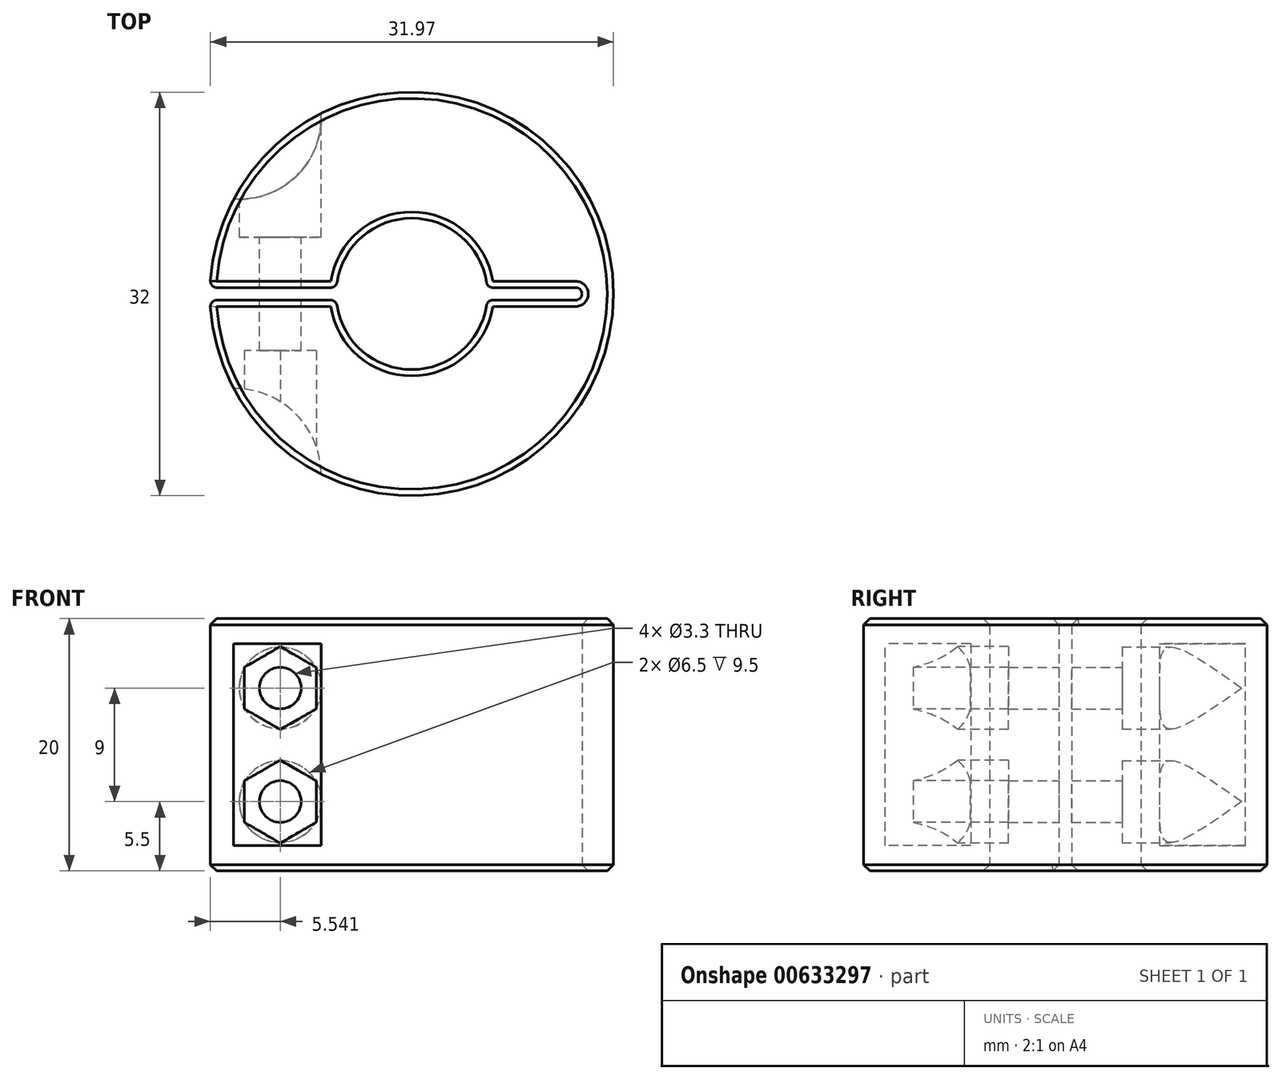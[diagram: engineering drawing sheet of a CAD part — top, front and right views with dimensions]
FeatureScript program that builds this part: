
annotation { "Feature Type Name" : "Feature", "Feature Type Description" : "" }
export const myFeature = defineFeature(function(context is Context, id is Id, definition is map)
    precondition{}
    {
        {
            var Q0;
            Q0=qCreatedBy(makeId("Top.planeOp"),FACE);
            var sketch = newSketch(context, id + "F0", { "sketchPlane" : qUnion([Q0])});
            skArc(sketch, "E0", {"start": v(5.93, 0.92) * mm, "mid": v(0, 6) * mm, "end": v(-5.93, 0.92) * mm});
            skArc(sketch, "E1.0", {"start": v(-15.97, -1.03) * mm, "mid": v(16, 0) * mm, "end": v(-15.97, 1.03) * mm});
            skLineSegment(sketch, "E2", {"start": v(6.42, 0.5) * mm, "end": v(13, 0.5) * mm});
            skLineSegment(sketch, "E3", {"start": v(13.5, 0) * mm, "end": v(13.5, 0) * mm});
            skLineSegment(sketch, "E4", {"start": v(13, -0.5) * mm, "end": v(6.42, -0.5) * mm});
            skPoint(sketch, "E5.visualSharp", {"position": v(13.5, 0.5) * mm});
            skArc(sketch, "E5.filletArc", {"start": v(13.5, 0) * mm, "mid": v(13.35, 0.35) * mm, "end": v(13, 0.5) * mm});
            skPoint(sketch, "E6.visualSharp", {"position": v(13.5, -0.5) * mm});
            skArc(sketch, "E6.filletArc", {"start": v(13, -0.5) * mm, "mid": v(13.35, -0.35) * mm, "end": v(13.5, 0) * mm});
            skPoint(sketch, "E7.visualSharp", {"position": v(5.98, 0.5) * mm});
            skArc(sketch, "E7.filletArc", {"start": v(5.93, 0.92) * mm, "mid": v(6.1, 0.62) * mm, "end": v(6.42, 0.5) * mm});
            skPoint(sketch, "E8.visualSharp", {"position": v(5.98, -0.5) * mm});
            skArc(sketch, "E8.filletArc", {"start": v(6.42, -0.5) * mm, "mid": v(6.1, -0.62) * mm, "end": v(5.93, -0.92) * mm});
            skLineSegment(sketch, "E9", {"start": v(-6.42, 0.5) * mm, "end": v(-15.47, 0.5) * mm});
            skLineSegment(sketch, "E10", {"start": v(-15.47, -0.5) * mm, "end": v(-6.42, -0.5) * mm});
            skArc(sketch, "E11.trimOffspring", {"start": v(-5.93, -0.92) * mm, "mid": v(0, -6) * mm, "end": v(5.93, -0.92) * mm});
            skPoint(sketch, "E12.visualSharp", {"position": v(-16, 0.5) * mm});
            skArc(sketch, "E12.filletArc", {"start": v(-15.97, 1.03) * mm, "mid": v(-15.83, 0.66) * mm, "end": v(-15.47, 0.5) * mm});
            skPoint(sketch, "E13.visualSharp", {"position": v(-16, -0.5) * mm});
            skArc(sketch, "E13.filletArc", {"start": v(-15.47, -0.5) * mm, "mid": v(-15.83, -0.66) * mm, "end": v(-15.97, -1.03) * mm});
            skPoint(sketch, "E14.visualSharp", {"position": v(-5.98, 0.5) * mm});
            skArc(sketch, "E14.filletArc", {"start": v(-6.42, 0.5) * mm, "mid": v(-6.1, 0.62) * mm, "end": v(-5.93, 0.92) * mm});
            skPoint(sketch, "E15.visualSharp", {"position": v(-5.98, -0.5) * mm});
            skArc(sketch, "E15.filletArc", {"start": v(-5.93, -0.92) * mm, "mid": v(-6.1, -0.62) * mm, "end": v(-6.42, -0.5) * mm});
            skSolve(sketch);
        }
        {
            var Q0;
            Q0=makeQuery(id+"F0.imprint","IMPRINT",FACE,{"disambiguationData":[TD([[makeQuery(id+"F0.imprint","IMPRINT",EDGE,{"derivedFrom":sQuery(id+"F0.wireOp",EDGE,"E0")}),-1.0]])]});
            extrude(context, id + "F1", {"entities" : qUnion([Q0]), "depth" : 20 * mm, "offsetDistance" : 25 * mm});
        }
        {
            var Q0;
            Q0=makeQuery(id+"F1.opExtrude","CAP_FACE",FACE,{"disambiguationData":[OSD([sQuery(id+"F0.wireOp",EDGE,"E0"),sQuery(id+"F0.wireOp",EDGE,"E1.0"),sQuery(id+"F0.wireOp",EDGE,"E2"),sQuery(id+"F0.wireOp",EDGE,"E4"),sQuery(id+"F0.wireOp",EDGE,"E5.filletArc"),sQuery(id+"F0.wireOp",EDGE,"E6.filletArc"),sQuery(id+"F0.wireOp",EDGE,"E7.filletArc"),sQuery(id+"F0.wireOp",EDGE,"E8.filletArc"),sQuery(id+"F0.wireOp",EDGE,"E9"),sQuery(id+"F0.wireOp",EDGE,"E10"),sQuery(id+"F0.wireOp",EDGE,"E11.trimOffspring"),sQuery(id+"F0.wireOp",EDGE,"E12.filletArc"),sQuery(id+"F0.wireOp",EDGE,"E13.filletArc"),sQuery(id+"F0.wireOp",EDGE,"E14.filletArc"),sQuery(id+"F0.wireOp",EDGE,"E15.filletArc")])],"isStart":false});
            var sketch = newSketch(context, id + "F2", { "sketchPlane" : qUnion([Q0])});
            skLineSegment(sketch, "E16.bottom", {"start": v(-13.68, 7.5) * mm, "end": v(-7.18, 7.5) * mm, "construction": true});
            skLineSegment(sketch, "E16.top", {"start": v(-13.68, 4.5) * mm, "end": v(-7.18, 4.5) * mm, "construction": true});
            skLineSegment(sketch, "E16.left", {"start": v(-13.68, 7.5) * mm, "end": v(-13.68, 4.5) * mm, "construction": true});
            skLineSegment(sketch, "E16.right", {"start": v(-7.18, 7.5) * mm, "end": v(-7.18, 4.5) * mm, "construction": true});
            skLineSegment(sketch, "E17.bottom", {"start": v(-11.93, 4.5) * mm, "end": v(-8.93, 4.5) * mm, "construction": true});
            skLineSegment(sketch, "E17.top", {"start": v(-11.93, -7.5) * mm, "end": v(-8.93, -7.5) * mm, "construction": true});
            skLineSegment(sketch, "E17.left", {"start": v(-11.93, 4.5) * mm, "end": v(-11.93, -7.5) * mm, "construction": true});
            skLineSegment(sketch, "E17.right", {"start": v(-8.93, 4.5) * mm, "end": v(-8.93, -7.5) * mm, "construction": true});
            skLineSegment(sketch, "E18", {"start": v(-10.43, -7.5) * mm, "end": v(-10.43, 6.38) * mm, "construction": true});
            skLineSegment(sketch, "E19", {"start": v(-13.68, -4.5) * mm, "end": v(-6.68, -4.5) * mm, "construction": true});
            skPoint(sketch, "E19.startSnap0", {"position": v(-13.68, 6) * mm});
            skLineSegment(sketch, "E20.bottom", {"start": v(-7.18, 7.5) * mm, "end": v(-15.38, 7.5) * mm});
            skLineSegment(sketch, "E20.top", {"start": v(-7.18, 14.57) * mm, "end": v(-15.38, 14.57) * mm});
            skLineSegment(sketch, "E20.left", {"start": v(-7.18, 7.5) * mm, "end": v(-7.18, 14.57) * mm});
            skLineSegment(sketch, "E20.right", {"start": v(-15.38, 7.5) * mm, "end": v(-15.38, 14.57) * mm});
            skLineSegment(sketch, "E21.bottom", {"start": v(-7.18, -7.5) * mm, "end": v(-17.74, -7.5) * mm});
            skLineSegment(sketch, "E21.top", {"start": v(-7.18, -14.68) * mm, "end": v(-17.74, -14.68) * mm});
            skLineSegment(sketch, "E21.left", {"start": v(-7.18, -7.5) * mm, "end": v(-7.18, -14.68) * mm});
            skLineSegment(sketch, "E21.right", {"start": v(-17.74, -7.5) * mm, "end": v(-17.74, -14.68) * mm});
            skSolve(sketch);
        }
        {
            var Q0;
            {var subQ0=sQuery(id+"F2.wireOp",EDGE,"E20.left");var subQ1=sQuery(id+"F2.wireOp",EDGE,"E20.bottom");var subQ2=makeQuery(id+"F2.imprint","INTERSECT",VERTEX,{"derivedFrom":[subQ1,subQ0]});Q0=makeQuery(id+"F2.imprint","IMPRINT",FACE,{"disambiguationData":[TD([[makeQuery(id+"F2.imprint","IMPRINT",EDGE,{"disambiguationData":[TD([[subQ2,-1.0]])],"derivedFrom":subQ1}),-1.0]])]});}
            var Q1;
            {var subQ0=sQuery(id+"F2.wireOp",EDGE,"E21.left");var subQ1=sQuery(id+"F2.wireOp",EDGE,"E21.bottom");var subQ2=makeQuery(id+"F2.imprint","INTERSECT",VERTEX,{"derivedFrom":[subQ1,subQ0]});Q1=makeQuery(id+"F2.imprint","IMPRINT",FACE,{"disambiguationData":[TD([[makeQuery(id+"F2.imprint","IMPRINT",EDGE,{"disambiguationData":[TD([[subQ2,-1.0]])],"derivedFrom":subQ1}),1.0]])]});}
            extrude(context, id + "F3", {"entities" : qUnion([Q0, Q1]), "operationType" : NewBodyOperationType.REMOVE, "oppositeDirection" : true, "depth" : 18 * mm, "offsetDistance" : 25 * mm, "hasSecondDirection" : true, "secondDirectionOppositeDirection" : true, "secondDirectionDepth" : 2 * mm});
        }
        {
            var Q0;
            Q0=makeQuery(id+"F3.boolean.opBoolean","COPY",FACE,{"derivedFrom":makeQuery(id+"F3.opExtrude","SWEPT_FACE",FACE,{"disambiguationData":[OSD([sQuery(id+"F2.wireOp",EDGE,"E20.bottom")])]})});
            var sketch = newSketch(context, id + "F4", { "sketchPlane" : qUnion([Q0])});
            skLineSegment(sketch, "E22", {"start": v(10.43, 18) * mm, "end": v(10.43, 2) * mm, "construction": true});
            skPoint(sketch, "E23", {"position": v(10.43, 14.5) * mm});
            skPoint(sketch, "E24", {"position": v(10.43, 5.5) * mm});
            skSolve(sketch);
        }
        {
            var Q0;
            Q0=sQuery(id+"F4.wireOp",VERTEX,"E23");
            var Q1;
            Q1=sQuery(id+"F4.wireOp",VERTEX,"E24");
            var Q2;
            Q2=makeQuery(id+"F1.opExtrude","SWEPT_BODY",BODY,{"disambiguationData":[OSD([sQuery(id+"F0.wireOp",EDGE,"E0"),sQuery(id+"F0.wireOp",EDGE,"E1.0"),sQuery(id+"F0.wireOp",EDGE,"E2"),sQuery(id+"F0.wireOp",EDGE,"E4"),sQuery(id+"F0.wireOp",EDGE,"E5.filletArc"),sQuery(id+"F0.wireOp",EDGE,"E6.filletArc"),sQuery(id+"F0.wireOp",EDGE,"E7.filletArc"),sQuery(id+"F0.wireOp",EDGE,"E8.filletArc"),sQuery(id+"F0.wireOp",EDGE,"E9"),sQuery(id+"F0.wireOp",EDGE,"E10"),sQuery(id+"F0.wireOp",EDGE,"E11.trimOffspring"),sQuery(id+"F0.wireOp",EDGE,"E12.filletArc"),sQuery(id+"F0.wireOp",EDGE,"E13.filletArc"),sQuery(id+"F0.wireOp",EDGE,"E14.filletArc"),sQuery(id+"F0.wireOp",EDGE,"E15.filletArc")])]});
            hole(context, id + "F5", {"style" : HoleStyle.C_BORE, "endStyle" : HoleEndStyle.THROUGH, "standardTappedOrClearance" : lookupTablePath({ "standard" : "ISO", "fit" : "Normal", "size" : "M3", "type" : "Clearance" }), "standardBlindInLast" : lookupTablePath({ "fit" : "Standard", "standard" : "ISO", "size" : "M3", "type" : "Clearance" }), "holeDiameter" : 3.3 * mm, "cBoreDiameter" : 6.5 * mm, "cBoreDepth" : 3 * mm, "majorDiameter" : 5 * mm, "isTappedThrough" : true, "tappedDepth" : 15 * mm, "tapClearance" : 0, "startFromSketch" : true, "locations" : qUnion([Q0, Q1]), "scope" : qUnion([Q2])});
        }
        {
            var Q0;
            Q0=makeQuery(id+"F3.boolean.opBoolean","COPY",FACE,{"derivedFrom":makeQuery(id+"F3.opExtrude","SWEPT_FACE",FACE,{"disambiguationData":[OSD([sQuery(id+"F2.wireOp",EDGE,"E21.bottom")])]})});
            var sketch = newSketch(context, id + "F6", { "sketchPlane" : qUnion([Q0])});
            skCircle(sketch, "E25.cCircle", {"center": v(-10.43, 14.5) * mm, "radius": 2.85 * mm, "construction": true});
            skLineSegment(sketch, "E25.0", {"start": v(-13.28, 12.85) * mm, "end": v(-13.28, 16.15) * mm});
            skLineSegment(sketch, "E25.1", {"start": v(-13.28, 16.15) * mm, "end": v(-10.43, 17.8) * mm});
            skLineSegment(sketch, "E25.2", {"start": v(-10.43, 17.8) * mm, "end": v(-7.58, 16.15) * mm});
            skLineSegment(sketch, "E25.3", {"start": v(-7.58, 16.15) * mm, "end": v(-7.58, 12.85) * mm});
            skLineSegment(sketch, "E25.4", {"start": v(-7.58, 12.85) * mm, "end": v(-10.43, 11.2) * mm});
            skLineSegment(sketch, "E25.5", {"start": v(-10.43, 11.2) * mm, "end": v(-13.28, 12.85) * mm});
            skPoint(sketch, "E25.0.midPoint", {"position": v(-13.28, 14.5) * mm});
            skCircle(sketch, "E26.cCircle", {"center": v(-10.43, 5.5) * mm, "radius": 2.85 * mm, "construction": true});
            skLineSegment(sketch, "E26.0", {"start": v(-13.28, 3.85) * mm, "end": v(-13.28, 7.15) * mm});
            skLineSegment(sketch, "E26.1", {"start": v(-13.28, 7.15) * mm, "end": v(-10.43, 8.8) * mm});
            skLineSegment(sketch, "E26.2", {"start": v(-10.43, 8.8) * mm, "end": v(-7.58, 7.15) * mm});
            skLineSegment(sketch, "E26.3", {"start": v(-7.58, 7.15) * mm, "end": v(-7.58, 3.85) * mm});
            skLineSegment(sketch, "E26.4", {"start": v(-7.58, 3.85) * mm, "end": v(-10.43, 2.2) * mm});
            skLineSegment(sketch, "E26.5", {"start": v(-10.43, 2.2) * mm, "end": v(-13.28, 3.85) * mm});
            skPoint(sketch, "E26.0.midPoint", {"position": v(-13.28, 5.5) * mm});
            skSolve(sketch);
        }
        {
            var Q0;
            Q0=makeQuery(id+"F6.imprint","IMPRINT",FACE,{"disambiguationData":[TD([[makeQuery(id+"F6.imprint","IMPRINT",EDGE,{"derivedFrom":sQuery(id+"F6.wireOp",EDGE,"E25.0")}),-1.0]])]});
            var Q1;
            Q1=makeQuery(id+"F6.imprint","IMPRINT",FACE,{"disambiguationData":[TD([[makeQuery(id+"F6.imprint","IMPRINT",EDGE,{"derivedFrom":sQuery(id+"F6.wireOp",EDGE,"E26.0")}),-1.0]])]});
            extrude(context, id + "F7", {"entities" : qUnion([Q0, Q1]), "operationType" : NewBodyOperationType.REMOVE, "oppositeDirection" : true, "depth" : 3 * mm, "offsetDistance" : 25 * mm});
        }
        {
            var Q0;
            {var subQ0=sQuery(id+"F2.wireOp",EDGE,"E20.bottom");var subQ2=sQuery(id+"F2.wireOp",EDGE,"E20.left");var subQ4=makeQuery(id+"F5.hole-0.opRevolve","SWEPT_FACE",FACE,{"disambiguationData":[OSD([sQuery(id+"F5.hole-0.sketch.wireOp",EDGE,"cbore_start_line_2")])]});Q0=makeQuery(id+"F5.hole-1.boolean.opBoolean","SPLIT",EDGE,{"disambiguationData":[TD([makeQuery(id+"F5.hole-0.boolean.opBoolean","COPY",FACE,{"derivedFrom":subQ4})])],"derivedFrom":makeQuery(id+"F5.hole-0.boolean.opBoolean","SPLIT",EDGE,{"disambiguationData":[TD([makeQuery(id+"F3.boolean.opBoolean","COPY",FACE,{"derivedFrom":makeQuery(id+"F3.opExtrude","CAP_FACE",FACE,{"disambiguationData":[OSD([sQuery(id+"F0.wireOp",EDGE,"E1.0"),subQ0,subQ2])],"isStart":false})})])],"derivedFrom":makeQuery(id+"F3.boolean.opBoolean","COPY",EDGE,{"derivedFrom":makeQuery(id+"F3.opExtrude","SWEPT_EDGE",EDGE,{"disambiguationData":[OSD([subQ0,subQ2])]})})})});}
            var Q1;
            {var subQ0=sQuery(id+"F2.wireOp",EDGE,"E20.bottom");var subQ1=sQuery(id+"F2.wireOp",EDGE,"E20.left");Q1=makeQuery(id+"F5.hole-0.boolean.opBoolean","SPLIT",EDGE,{"disambiguationData":[TD([makeQuery(id+"F3.boolean.opBoolean","COPY",FACE,{"derivedFrom":makeQuery(id+"F3.opExtrude","CAP_FACE",FACE,{"disambiguationData":[OSD([sQuery(id+"F0.wireOp",EDGE,"E1.0"),subQ0,subQ1])],"isStart":true})})])],"derivedFrom":makeQuery(id+"F3.boolean.opBoolean","COPY",EDGE,{"derivedFrom":makeQuery(id+"F3.opExtrude","SWEPT_EDGE",EDGE,{"disambiguationData":[OSD([subQ0,subQ1])]})})});}
            var Q2;
            {var subQ0=sQuery(id+"F2.wireOp",EDGE,"E20.bottom");var subQ2=sQuery(id+"F2.wireOp",EDGE,"E20.left");var subQ3=makeQuery(id+"F3.boolean.opBoolean","COPY",FACE,{"derivedFrom":makeQuery(id+"F3.opExtrude","CAP_FACE",FACE,{"disambiguationData":[OSD([sQuery(id+"F0.wireOp",EDGE,"E1.0"),subQ0,subQ2])],"isStart":false})});Q2=makeQuery(id+"F5.hole-1.boolean.opBoolean","SPLIT",EDGE,{"disambiguationData":[TD([subQ3])],"derivedFrom":makeQuery(id+"F5.hole-0.boolean.opBoolean","SPLIT",EDGE,{"disambiguationData":[TD([subQ3])],"derivedFrom":makeQuery(id+"F3.boolean.opBoolean","COPY",EDGE,{"derivedFrom":makeQuery(id+"F3.opExtrude","SWEPT_EDGE",EDGE,{"disambiguationData":[OSD([subQ0,subQ2])]})})})});}
            fillet(context, id + "F8", {"entities" : qUnion([Q0, Q1, Q2]), "radius" : 6.5 * mm, "tangentPropagation" : true, "allowEdgeOverflow" : false});
        }
        {
            var Q0;
            Q0=makeQuery(id+"F3.boolean.opBoolean","COPY",EDGE,{"derivedFrom":makeQuery(id+"F3.opExtrude","SWEPT_EDGE",EDGE,{"disambiguationData":[OSD([sQuery(id+"F2.wireOp",EDGE,"E21.bottom"),sQuery(id+"F2.wireOp",EDGE,"E21.left")])]})});
            fillet(context, id + "F9", {"entities" : qUnion([Q0]), "radius" : 6.9 * mm, "tangentPropagation" : true, "allowEdgeOverflow" : false});
        }
        {
            var Q0;
            Q0=makeQuery(id+"F1.opExtrude","CAP_EDGE",EDGE,{"disambiguationData":[OSD([sQuery(id+"F0.wireOp",EDGE,"E1.0")])],"isStart":true});
            var Q1;
            Q1=makeQuery(id+"F1.opExtrude","CAP_EDGE",EDGE,{"disambiguationData":[OSD([sQuery(id+"F0.wireOp",EDGE,"E1.0")])],"isStart":false});
            chamfer(context, id + "F10", {"entities" : qUnion([Q0, Q1]), "width" : .5 * mm, "tangentPropagation" : true});
        }
    });
